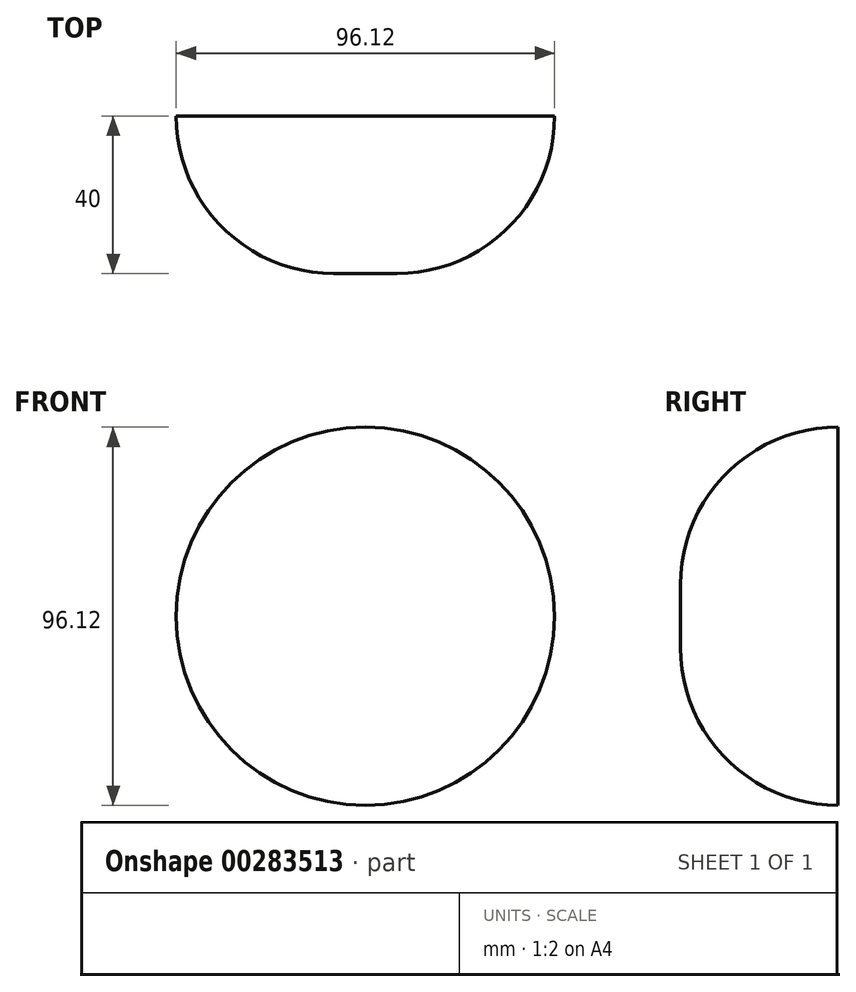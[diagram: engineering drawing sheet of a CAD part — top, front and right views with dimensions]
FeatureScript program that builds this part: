
annotation { "Feature Type Name" : "Feature", "Feature Type Description" : "" }
export const myFeature = defineFeature(function(context is Context, id is Id, definition is map)
    precondition{}
    {
        {
            var Q0;
            Q0=qCreatedBy(makeId("Front.planeOp"),FACE);
            var sketch = newSketch(context, id + "F0", { "sketchPlane" : qUnion([Q0])});
            skCircle(sketch, "E0", {"center": v(0, 0) * mm, "radius": 48.06 * mm});
            skSolve(sketch);
        }
        {
            var Q0;
            Q0 = qSketchRegion(id + "F0", true);
            extrude(context, id + "F1", {"entities" : qUnion([Q0]), "endBound" : BoundingType.SYMMETRIC, "depth" : 40 * mm});
        }
        {
            var Q0;
            Q0=makeQuery(id+"F1.opExtrude","CAP_EDGE",EDGE,{"disambiguationData":[OSD([sQuery(id+"F0.wireOp",EDGE,"E0")])],"isStart":false});
            fillet(context, id + "F2", {"entities" : qUnion([Q0]), "radius" : 40 * mm, "tangentPropagation" : true, "allowEdgeOverflow" : false});
        }
    });
